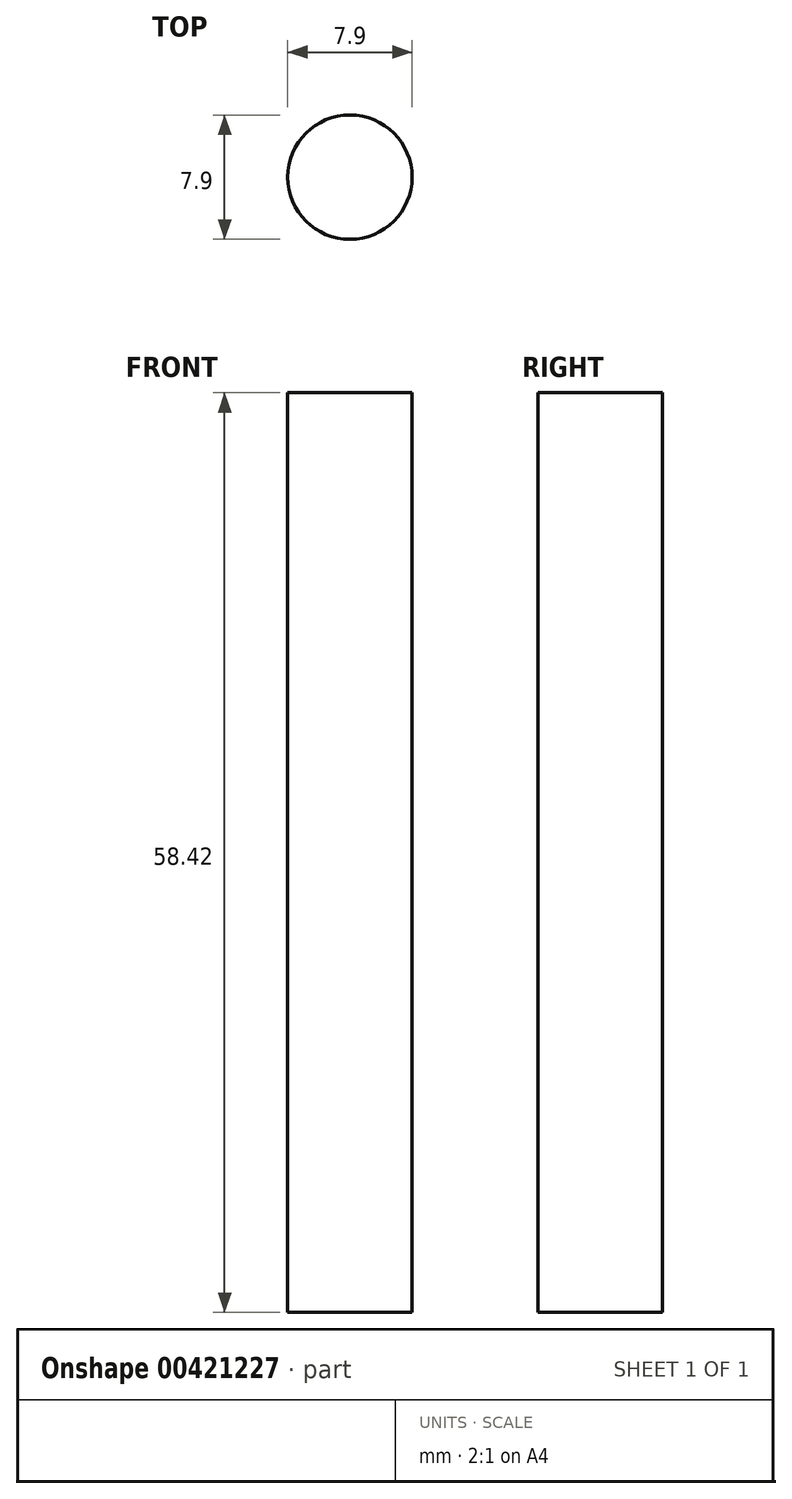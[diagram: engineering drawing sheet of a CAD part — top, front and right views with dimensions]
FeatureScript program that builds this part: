
annotation { "Feature Type Name" : "Feature", "Feature Type Description" : "" }
export const myFeature = defineFeature(function(context is Context, id is Id, definition is map)
    precondition{}
    {
        {
            var Q0;
            Q0=qCreatedBy(makeId("Top.planeOp"),FACE);
            var sketch = newSketch(context, id + "F0", { "sketchPlane" : qUnion([Q0])});
            skCircle(sketch, "E0", {"center": v(0, 0) * mm, "radius": 3.95 * mm});
            skSolve(sketch);
        }
        {
            var Q0;
            Q0 = qSketchRegion(id + "F0", true);
            extrude(context, id + "F1", {"entities" : qUnion([Q0]), "depth" : 58.42 * mm});
        }
    });
